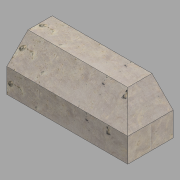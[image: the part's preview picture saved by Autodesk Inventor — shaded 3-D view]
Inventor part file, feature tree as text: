
AUTODESK INVENTOR PART (.ipt)
format: ipt  version: 2022.1 (Build 261234020, 234B)  size: 127,488 bytes
history: native  units: in
note: dims shown in document units (in); Inventor stores cm internally (conversion verified against a paired STEP export)
features: other x3, mirror x1
ambient origin geometry x8: Origin, YZ Plane, XZ Plane, XY Plane, X Axis, Y Axis, Z Axis, Center Point
bodies: Solid1 (feature_tree)
feature tree (4):
  other  "Return_L.ipt"
  mirror  "Mirror1"
  other  "Solid1::Return_L.ipt"
  other  "TaggingFeature1"
